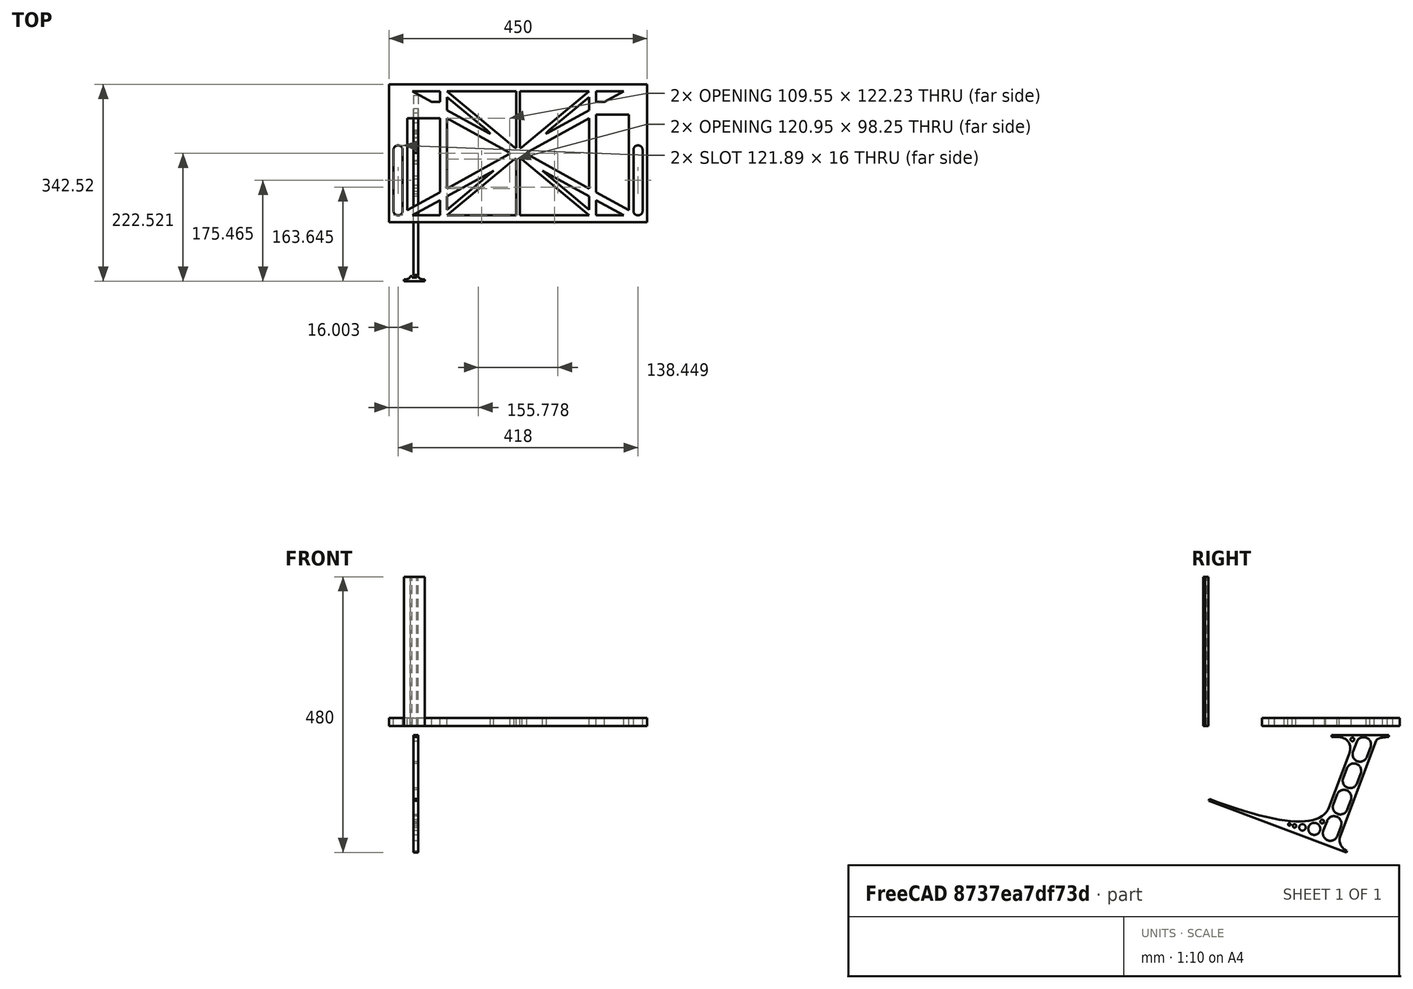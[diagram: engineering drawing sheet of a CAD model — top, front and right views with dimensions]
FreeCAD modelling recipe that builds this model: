
FCSTD DOCUMENT  (FreeCAD 0.19R0.19.2)
Label: laptopStand066
License: All rights reserved
LicenseURL: http://en.wikipedia.org/wiki/All_rights_reserved
objects: Sketcher::SketchObject×3, Part::Extrusion×3
note: 6 computed .brp shape members not serialized (recipe doc carries the construction recipe); baked Part::Feature solids carry a one-line shape summary decoded from their .brp

FEATURE [Sketcher::SketchObject] Sketch
  FullyConstrained = true
  sketch-geometry (112):
    g0: LineSegment StartX=-10.9272 StartY=-82.7794 StartZ=0 EndX=46.0728 EndY=-51.4823 EndZ=0
    g1: LineSegment StartX=366.073 StartY=-91.7794 StartZ=0 EndX=318.073 EndY=-65.424 EndZ=0
    g2: LineSegment StartX=-10.9272 StartY=77.3346 StartZ=0 EndX=-10.9272 EndY=-82.7794 EndZ=0
    g3: LineSegment StartX=375.073 StartY=-82.7794 StartZ=0 EndX=375.073 EndY=83.9235 EndZ=0
    g4: LineSegment StartX=-1.92719 StartY=-91.7794 StartZ=0 EndX=46.0728 EndY=-91.7794 EndZ=0
    g5: LineSegment StartX=318.073 StartY=124.221 StartZ=0 EndX=366.073 EndY=124.221 EndZ=0
    g6: LineSegment StartX=306.073 StartY=-81.8102 StartZ=0 EndX=224.513 EndY=-14.0532 EndZ=0
    g7: LineSegment StartX=306.073 StartY=124.221 StartZ=0 EndX=189.124 EndY=27.0628 EndZ=0
    g8: LineSegment StartX=58.0728 StartY=-91.7794 StartZ=0 EndX=175.022 EndY=5.37834 EndZ=0
    g9: LineSegment StartX=58.0728 StartY=-81.8102 StartZ=0 EndX=58.0728 EndY=-58.8351 EndZ=0
    g10: LineSegment StartX=306.073 StartY=114.251 StartZ=0 EndX=306.073 EndY=91.2763 EndZ=0
    g11: LineSegment StartX=175.022 StartY=27.0628 StartZ=0 EndX=58.0728 EndY=124.221 EndZ=0
    g12: LineSegment StartX=139.632 StartY=-14.0532 StartZ=0 EndX=58.0728 EndY=-81.8102 EndZ=0
    g13: LineSegment StartX=139.632 StartY=-14.0532 StartZ=0 EndX=58.0728 EndY=-58.8351 EndZ=0
    g14: LineSegment StartX=189.124 StartY=5.37834 StartZ=0 EndX=306.073 EndY=-91.7794 EndZ=0
    g15: LineSegment StartX=306.073 StartY=77.3346 StartZ=0 EndX=306.073 EndY=-44.8935 EndZ=0
    g16: LineSegment StartX=318.073 StartY=83.9235 StartZ=0 EndX=318.073 EndY=-51.4823 EndZ=0
    g17: LineSegment StartX=306.073 StartY=-58.8351 StartZ=0 EndX=224.513 EndY=-14.0532 EndZ=0
    g18: LineSegment StartX=306.073 StartY=-58.8351 StartZ=0 EndX=306.073 EndY=-81.8102 EndZ=0
    g19: LineSegment StartX=318.073 StartY=-51.4823 StartZ=0 EndX=375.073 EndY=-82.7794 EndZ=0
    g20: LineSegment StartX=318.073 StartY=-65.424 StartZ=0 EndX=318.073 EndY=-91.7794 EndZ=0
    g21: LineSegment StartX=318.073 StartY=-91.7794 StartZ=0 EndX=366.073 EndY=-91.7794 EndZ=0
    g22: LineSegment StartX=58.0728 StartY=-44.8935 StartZ=0 EndX=58.0728 EndY=77.3346 EndZ=0
    g23: LineSegment StartX=46.0728 StartY=-65.424 StartZ=0 EndX=-1.92719 EndY=-91.7794 EndZ=0
    g24: LineSegment StartX=46.0728 StartY=-65.424 StartZ=0 EndX=46.0728 EndY=-91.7794 EndZ=0
    g25: LineSegment StartX=58.0728 StartY=91.2763 StartZ=0 EndX=58.0728 EndY=114.251 EndZ=0
    g26: LineSegment StartX=46.0728 StartY=77.3346 StartZ=0 EndX=46.0728 EndY=-51.4823 EndZ=0
    g27: LineSegment StartX=-42.9272 StartY=136.221 StartZ=0 EndX=-42.9272 EndY=-103.779 EndZ=0
    g28: LineSegment StartX=407.073 StartY=136.221 StartZ=0 EndX=407.073 EndY=-103.779 EndZ=0
    g29: LineSegment StartX=179.022 StartY=27.0628 StartZ=0 EndX=179.022 EndY=124.221 EndZ=0
    g30: LineSegment StartX=185.124 StartY=27.0628 StartZ=0 EndX=185.124 EndY=124.221 EndZ=0
    g31: ArcOfCircle CenterX=-26.9272 CenterY=22.1087 CenterZ=0 NormalX=0 NormalY=0 NormalZ=1 AngleXU=0 Radius=8 StartAngle=1e-16 EndAngle=3.14159
    g32: ArcOfCircle CenterX=-26.9272 CenterY=-83.7794 CenterZ=0 NormalX=0 NormalY=0 NormalZ=1 AngleXU=0 Radius=8 StartAngle=3.14159 EndAngle=6.28319
    g33: LineSegment StartX=-34.9272 StartY=22.1087 StartZ=0 EndX=-34.9272 EndY=-83.7794 EndZ=0
    g34: LineSegment StartX=-18.9272 StartY=22.1087 StartZ=0 EndX=-18.9272 EndY=-83.7794 EndZ=0
    g35: LineSegment StartX=185.124 StartY=-91.7794 StartZ=0 EndX=306.073 EndY=-91.7794 EndZ=0
    g36: LineSegment StartX=179.022 StartY=-91.7794 StartZ=0 EndX=58.0728 EndY=-91.7794 EndZ=0
    g37: LineSegment StartX=306.073 StartY=124.221 StartZ=0 EndX=185.124 EndY=124.221 EndZ=0
    g38: LineSegment StartX=179.022 StartY=124.221 StartZ=0 EndX=58.0728 EndY=124.221 EndZ=0
    g39: ArcOfCircle CenterX=391.073 CenterY=22.1087 CenterZ=0 NormalX=0 NormalY=0 NormalZ=1 AngleXU=0 Radius=8 StartAngle=-4.4e-15 EndAngle=3.14159
    g40: LineSegment StartX=399.073 StartY=22.1087 StartZ=0 EndX=399.073 EndY=-83.7794 EndZ=0
    g41: LineSegment StartX=383.073 StartY=22.1087 StartZ=0 EndX=383.073 EndY=-83.7794 EndZ=0
    g42: ArcOfCircle CenterX=391.073 CenterY=-83.7794 CenterZ=0 NormalX=0 NormalY=0 NormalZ=1 AngleXU=0 Radius=8 StartAngle=3.14159 EndAngle=6.28319
    g43: Circle CenterX=175.022 CenterY=27.0628 CenterZ=0 NormalX=0 NormalY=0 NormalZ=1 AngleXU=0 Radius=1
    g44: Circle CenterX=179.022 CenterY=24.8665 CenterZ=0 NormalX=0 NormalY=0 NormalZ=1 AngleXU=0 Radius=1
    g45: Circle CenterX=179.022 CenterY=27.0628 CenterZ=0 NormalX=0 NormalY=0 NormalZ=1 AngleXU=0 Radius=1
    g46: BSplineCurve PolesCount=3 KnotsCount=2 Degree=2 IsPeriodic=0
    g47: GeomPoint X=175.022 Y=27.0628 Z=0
    g48: GeomPoint X=179.022 Y=27.0628 Z=0
    g49: Circle CenterX=189.124 CenterY=27.0628 CenterZ=0 NormalX=0 NormalY=0 NormalZ=1 AngleXU=0 Radius=1
    g50: Circle CenterX=185.124 CenterY=24.8665 CenterZ=0 NormalX=0 NormalY=0 NormalZ=1 AngleXU=0 Radius=1
    g51: Circle CenterX=185.124 CenterY=27.0628 CenterZ=0 NormalX=0 NormalY=0 NormalZ=1 AngleXU=0 Radius=1
    g52: BSplineCurve PolesCount=3 KnotsCount=2 Degree=2 IsPeriodic=0
    g53: GeomPoint X=189.124 Y=27.0628 Z=0
    g54: GeomPoint X=185.124 Y=27.0628 Z=0
    g55: Circle CenterX=175.022 CenterY=5.37834 CenterZ=0 NormalX=0 NormalY=0 NormalZ=1 AngleXU=0 Radius=1
    g56: Circle CenterX=179.022 CenterY=7.57463 CenterZ=0 NormalX=0 NormalY=0 NormalZ=1 AngleXU=0 Radius=1
    g57: Circle CenterX=179.022 CenterY=5.34704 CenterZ=0 NormalX=0 NormalY=0 NormalZ=1 AngleXU=0 Radius=1
    g58: BSplineCurve PolesCount=3 KnotsCount=2 Degree=2 IsPeriodic=0
    g59: GeomPoint X=175.022 Y=5.37834 Z=0
    g60: GeomPoint X=179.022 Y=5.34704 Z=0
    g61: Circle CenterX=189.124 CenterY=5.37834 CenterZ=0 NormalX=0 NormalY=0 NormalZ=1 AngleXU=0 Radius=1
    g62: Circle CenterX=185.124 CenterY=7.57463 CenterZ=0 NormalX=0 NormalY=0 NormalZ=1 AngleXU=0 Radius=1
    g63: Circle CenterX=185.124 CenterY=5.34704 CenterZ=0 NormalX=0 NormalY=0 NormalZ=1 AngleXU=0 Radius=1
    g64: BSplineCurve PolesCount=3 KnotsCount=2 Degree=2 IsPeriodic=0
    g65: GeomPoint X=189.124 Y=5.37834 Z=0
    g66: GeomPoint X=185.124 Y=5.34704 Z=0
    g67: LineSegment StartX=179.022 StartY=5.34704 StartZ=0 EndX=179.022 EndY=-91.7794 EndZ=0
    g68: LineSegment StartX=185.124 StartY=-91.7794 StartZ=0 EndX=185.124 EndY=5.34704 EndZ=0
    g69: Circle CenterX=165.871 CenterY=18.1458 CenterZ=0 NormalX=0 NormalY=0 NormalZ=1 AngleXU=0 Radius=1
    g70: Circle CenterX=169.377 CenterY=16.2206 CenterZ=0 NormalX=0 NormalY=0 NormalZ=1 AngleXU=0 Radius=1
    g71: Circle CenterX=165.871 CenterY=14.2954 CenterZ=0 NormalX=0 NormalY=0 NormalZ=1 AngleXU=0 Radius=1
    g72: BSplineCurve PolesCount=3 KnotsCount=2 Degree=2 IsPeriodic=0
    g73: GeomPoint X=165.871 Y=18.1458 Z=0
    g74: GeomPoint X=165.871 Y=14.2954 Z=0
    g75: Circle CenterX=198.275 CenterY=18.1458 CenterZ=0 NormalX=0 NormalY=0 NormalZ=1 AngleXU=0 Radius=1
    g76: Circle CenterX=194.768 CenterY=16.2206 CenterZ=0 NormalX=0 NormalY=0 NormalZ=1 AngleXU=0 Radius=1
    g77: Circle CenterX=198.275 CenterY=14.2954 CenterZ=0 NormalX=0 NormalY=0 NormalZ=1 AngleXU=0 Radius=1
    g78: BSplineCurve PolesCount=3 KnotsCount=2 Degree=2 IsPeriodic=0
    g79: GeomPoint X=198.275 Y=18.1458 Z=0
    g80: GeomPoint X=198.275 Y=14.2954 Z=0
    g81: LineSegment StartX=165.871 StartY=18.1458 StartZ=0 EndX=58.0728 EndY=77.3346 EndZ=0
    g82: LineSegment StartX=58.0728 StartY=-44.8935 StartZ=0 EndX=165.871 EndY=14.2954 EndZ=0
    g83: LineSegment StartX=198.275 StartY=18.1458 StartZ=0 EndX=306.073 EndY=77.3346 EndZ=0
    g84: LineSegment StartX=198.275 StartY=14.2954 StartZ=0 EndX=306.073 EndY=-44.8935 EndZ=0
    g85: LineSegment StartX=407.073 StartY=-103.779 StartZ=0 EndX=-42.9272 EndY=-103.779 EndZ=0
    g86: LineSegment StartX=407.073 StartY=136.221 StartZ=0 EndX=-42.9272 EndY=136.221 EndZ=0
    g87: LineSegment StartX=46.0728 StartY=77.3346 StartZ=0 EndX=-10.9272 EndY=77.3346 EndZ=0
    g88: LineSegment StartX=46.0728 StartY=105.865 StartZ=0 EndX=31.5028 EndY=105.865 EndZ=0
    g89: LineSegment StartX=46.0728 StartY=124.221 StartZ=0 EndX=46.0728 EndY=105.865 EndZ=0
    g90: LineSegment StartX=-1.92719 StartY=124.221 StartZ=0 EndX=31.5028 EndY=105.865 EndZ=0
    g91: LineSegment StartX=46.0728 StartY=124.221 StartZ=0 EndX=-1.92719 EndY=124.221 EndZ=0
    g92: LineSegment StartX=318.073 StartY=83.9235 StartZ=0 EndX=375.073 EndY=83.9235 EndZ=0
    g93: LineSegment StartX=318.073 StartY=105.865 StartZ=0 EndX=332.643 EndY=105.865 EndZ=0
    g94: LineSegment StartX=332.643 StartY=105.865 StartZ=0 EndX=366.073 EndY=124.221 EndZ=0
    g95: LineSegment StartX=318.073 StartY=124.221 StartZ=0 EndX=318.073 EndY=105.865 EndZ=0
    g96: Circle CenterX=125.607 CenterY=54.1951 CenterZ=0 NormalX=0 NormalY=0 NormalZ=1 AngleXU=0 Radius=1
    g97: Circle CenterX=139.632 CenterY=46.4944 CenterZ=0 NormalX=0 NormalY=0 NormalZ=1 AngleXU=0 Radius=1
    g98: Circle CenterX=127.325 CenterY=56.7187 CenterZ=0 NormalX=0 NormalY=0 NormalZ=1 AngleXU=0 Radius=1
    g99: BSplineCurve PolesCount=3 KnotsCount=2 Degree=2 IsPeriodic=0
    g100: GeomPoint X=125.607 Y=54.1951 Z=0
    g101: GeomPoint X=127.325 Y=56.7187 Z=0
    g102: LineSegment StartX=127.325 StartY=56.7187 StartZ=0 EndX=58.0728 EndY=114.251 EndZ=0
    g103: LineSegment StartX=58.0728 StartY=91.2763 StartZ=0 EndX=125.607 EndY=54.1951 EndZ=0
    g104: Circle CenterX=236.821 CenterY=56.7187 CenterZ=0 NormalX=0 NormalY=0 NormalZ=1 AngleXU=0 Radius=1
    g105: Circle CenterX=224.513 CenterY=46.4944 CenterZ=0 NormalX=0 NormalY=0 NormalZ=1 AngleXU=0 Radius=1
    g106: Circle CenterX=238.538 CenterY=54.1951 CenterZ=0 NormalX=0 NormalY=0 NormalZ=1 AngleXU=0 Radius=1
    g107: BSplineCurve PolesCount=3 KnotsCount=2 Degree=2 IsPeriodic=0
    g108: GeomPoint X=236.821 Y=56.7187 Z=0
    g109: GeomPoint X=238.538 Y=54.1951 Z=0
    g110: LineSegment StartX=236.821 StartY=56.7187 StartZ=0 EndX=306.073 EndY=114.251 EndZ=0
    g111: LineSegment StartX=238.538 StartY=54.1951 StartZ=0 EndX=306.073 EndY=91.2763 EndZ=0
  constraints (207):
    c: Horizontal(g4)
    c: Horizontal(g5)
    c: Coincident(g13,g12)
    c: Coincident(g17,g6)
    c: Tangent(g10,g15)
    c: Coincident(g18,g6)
    c: Tangent(g1,g17)
    c: Tangent(g15,g18)
    c: Coincident(g16,g19)
    c: Coincident(g20,g1)
    c: Tangent(g16,g20)
    c: Coincident(g12,g9)
    c: Tangent(g9,g22)
    c: Coincident(g13,g9)
    c: Tangent(g13,g23)
    c: Coincident(g24,g23)
    c: Coincident(g0,g26)
    c: Tangent(g22,g25)
    c: Block(g11)
    c: Block(g7)
    c: Block(g19)
    c: Block(g3)
    c: Block(g17)
    c: Block(g18)
    c: Block(g1)
    c: Block(g20)
    c: Block(g14)
    c: Block(g8)
    c: Block(g13)
    c: Block(g12)
    c: Block(g24)
    c: Block(g23)
    c: Block(g0)
    c: Block(g2)
    c: Block(g25)
    c: Block(g15)
    c: Block(g5)
    c: Block(g21)
    c: Block(g4)
    c: Vertical(g27)
    c: Vertical(g28)
    c: Block(g28)
    c: Block(g27)
    c: Vertical(g29)
    c: Vertical(g30)
    c: Block(g29)
    c: Block(g30)
    c: Tangent(g31,g34) = 1.5708
    c: Tangent(g31,g33) = -1.5708
    c: Tangent(g33,g32) = -1.5708
    c: Tangent(g34,g32) = 1.5708
    c: Vertical(g33)
    c: Equal(g31,g32)
    c: Block(g34)
    c: Block(g33)
    c: Coincident(g35,g14)
    c: Horizontal(g35)
    c: Coincident(g36,g8)
    c: Horizontal(g36)
    c: Coincident(g37,g7)
    c: Coincident(g37,g30)
    c: Horizontal(g37)
    c: Coincident(g38,g29)
    c: Coincident(g38,g11)
    c: Horizontal(g38)
    c: Tangent(g39,g40) = 1.5708
    c: Tangent(g40,g42) = 1.5708
    c: Equal(g39,g42)
    c: Coincident(g41,g39)
    c: Coincident(g41,g42)
    c: Block(g40)
    c: Block(g41)
    c: Coincident(g46,g11)
    c: Weight(g43) = 1
    c: Equal(g43,g44)
    c: Equal(g43,g45)
    c: Coincident(g46,g29)
    c: InternalAlignment(g43,g46)
    c: InternalAlignment(g44,g46)
    c: InternalAlignment(g45,g46)
    c: InternalAlignment(g47,g46)
    c: InternalAlignment(g48,g46)
    c: Coincident(g52,g7)
    c: Weight(g49) = 1
    c: Equal(g49,g50)
    c: Equal(g49,g51)
    c: Coincident(g52,g30)
    c: InternalAlignment(g49,g52)
    c: InternalAlignment(g50,g52)
    c: InternalAlignment(g51,g52)
    c: InternalAlignment(g53,g52)
    c: InternalAlignment(g54,g52)
    c: Block(g52)
    c: Block(g46)
    c: Coincident(g58,g8)
    c: Weight(g55) = 1
    c: Equal(g55,g56)
    c: Equal(g55,g57)
    c: InternalAlignment(g55,g58)
    c: InternalAlignment(g56,g58)
    c: InternalAlignment(g57,g58)
    c: InternalAlignment(g59,g58)
    c: InternalAlignment(g60,g58)
    c: Weight(g61) = 1
    c: Equal(g61,g62)
    c: Equal(g61,g63)
    c: InternalAlignment(g61,g64)
    c: InternalAlignment(g62,g64)
    c: InternalAlignment(g63,g64)
    c: InternalAlignment(g65,g64)
    c: InternalAlignment(g66,g64)
    c: Block(g64)
    c: Block(g58)
    c: Coincident(g67,g58)
    c: Coincident(g67,g36)
    c: Vertical(g67)
    c: Coincident(g68,g35)
    c: Coincident(g68,g64)
    c: Vertical(g68)
    c: Weight(g69) = 1
    c: Equal(g69,g70)
    c: Equal(g69,g71)
    c: InternalAlignment(g69,g72)
    c: InternalAlignment(g70,g72)
    c: InternalAlignment(g71,g72)
    c: InternalAlignment(g73,g72)
    c: InternalAlignment(g74,g72)
    c: Weight(g75) = 1
    c: Equal(g75,g76)
    c: Equal(g75,g77)
    c: InternalAlignment(g75,g78)
    c: InternalAlignment(g76,g78)
    c: InternalAlignment(g77,g78)
    c: InternalAlignment(g79,g78)
    c: InternalAlignment(g80,g78)
    c: Block(g72)
    c: Block(g78)
    c: Coincident(g81,g72)
    c: Coincident(g81,g22)
    c: Coincident(g82,g22)
    c: Coincident(g82,g72)
    c: Coincident(g83,g78)
    c: Coincident(g83,g15)
    c: Coincident(g84,g78)
    c: Coincident(g84,g15)
    c: Block(g22)
    c: Coincident(g85,g28)
    c: Coincident(g85,g27)
    c: Horizontal(g85)
    c: Distance(g85) = 450
    c: Coincident(g86,g28)
    c: Coincident(g86,g27)
    c: Horizontal(g86)
    c: Horizontal(g87)
    c: Coincident(g26,g87)
    c: Horizontal(g88)
    c: Vertical(g89)
    c: Block(g89)
    c: Block(g88)
    c: Block(g87)
    c: Distance(g89) = 18.3554
    c: Coincident(g91,g89)
    c: Coincident(g91,g90)
    c: Horizontal(g91)
    c: Block(g91)
    c: Block(g90)
    c: Coincident(g88,g90)
    c: Coincident(g2,g87)
    c: Coincident(g92,g16)
    c: Horizontal(g92)
    c: Horizontal(g93)
    c: Block(g92)
    c: Block(g10)
    c: Coincident(g94,g5)
    c: Coincident(g95,g5)
    c: Coincident(g95,g93)
    c: Vertical(g95)
    c: Block(g95)
    c: Coincident(g93,g94)
    c: Block(g94)
    c: Coincident(g3,g92)
    c: Weight(g96) = 1
    c: Equal(g96,g97)
    c: Equal(g96,g98)
    c: InternalAlignment(g96,g99)
    c: InternalAlignment(g97,g99)
    c: InternalAlignment(g98,g99)
    c: InternalAlignment(g100,g99)
    c: InternalAlignment(g101,g99)
    c: Block(g99)
    c: Coincident(g102,g99)
    c: Coincident(g102,g25)
    c: Coincident(g103,g25)
    c: Coincident(g103,g99)
    c: Weight(g104) = 1
    c: Equal(g104,g105)
    c: Equal(g104,g106)
    c: InternalAlignment(g104,g107)
    c: InternalAlignment(g105,g107)
    c: InternalAlignment(g106,g107)
    c: InternalAlignment(g108,g107)
    c: InternalAlignment(g109,g107)
    c: Block(g107)
    c: Coincident(g110,g107)
    c: Coincident(g110,g10)
    c: Coincident(g111,g107)
    c: Coincident(g111,g10)
FEATURE [Sketcher::SketchObject] Sketch001
  FullyConstrained = true
  MapMode = 4
  Placement = pos=(0,0,0) rot=(0.57735,0.57735,0.57735;2.0944rad)
  Support = -> [Sketch]
  sketch-geometry (46):
    g0: BSplineCurve PolesCount=3 KnotsCount=2 Degree=2 IsPeriodic=0
    g1: ArcOfCircle CenterX=73.1223 CenterY=-32.291 CenterZ=0 NormalX=0 NormalY=0 NormalZ=1 AngleXU=0 Radius=13 StartAngle=5.92268 EndAngle=9.06428
    g2: ArcOfCircle CenterX=66.7816 CenterY=-49.1439 CenterZ=0 NormalX=0 NormalY=0 NormalZ=1 AngleXU=0 Radius=13 StartAngle=2.78068 EndAngle=5.92131
    g3: ArcOfCircle CenterX=55.9263 CenterY=-78.1807 CenterZ=0 NormalX=0 NormalY=0 NormalZ=1 AngleXU=0 Radius=13 StartAngle=5.92268 EndAngle=9.06428
    g4: ArcOfCircle CenterX=49.5884 CenterY=-95.0342 CenterZ=0 NormalX=0 NormalY=0 NormalZ=1 AngleXU=0 Radius=13 StartAngle=2.78068 EndAngle=5.92131
    g5: ArcOfCircle CenterX=38.7206 CenterY=-124.067 CenterZ=0 NormalX=0 NormalY=0 NormalZ=1 AngleXU=0 Radius=13 StartAngle=5.92268 EndAngle=9.06428
    g6: ArcOfCircle CenterX=32.3875 CenterY=-140.92 CenterZ=0 NormalX=0 NormalY=0 NormalZ=1 AngleXU=0 Radius=13 StartAngle=2.78068 EndAngle=5.92131
    g7: ArcOfCircle CenterX=21.4715 CenterY=-169.934 CenterZ=0 NormalX=0 NormalY=0 NormalZ=1 AngleXU=0 Radius=13 StartAngle=5.92268 EndAngle=9.06428
    g8: ArcOfCircle CenterX=15.1336 CenterY=-186.787 CenterZ=0 NormalX=0 NormalY=0 NormalZ=1 AngleXU=0 Radius=13 StartAngle=2.78068 EndAngle=5.92131
    g9-g12: Circle x4 (B-spline internal-alignment scaffolding for g13; pole/knot coordinates omitted)
    g13: BSplineCurve PolesCount=4 KnotsCount=2 Degree=3 IsPeriodic=0
    g14: GeomPoint X=28.8094 Y=-19.0875 Z=0
    g15: GeomPoint X=47.0443 Y=-50.4712 Z=0
    g16: Circle CenterX=53.5586 CenterY=-23.2695 CenterZ=0 NormalX=0 NormalY=0 NormalZ=1 AngleXU=0 Radius=3.24518
    g17: Circle CenterX=-195.441 CenterY=-127.082 CenterZ=0 NormalX=0 NormalY=0 NormalZ=1 AngleXU=0 Radius=1
    g18: Circle CenterX=-8.24091 CenterY=-197.481 CenterZ=0 NormalX=0 NormalY=0 NormalZ=1 AngleXU=0 Radius=1
    g19: Circle CenterX=12.8789 CenterY=-141.321 CenterZ=0 NormalX=0 NormalY=0 NormalZ=1 AngleXU=0 Radius=1
    g20: BSplineCurve PolesCount=3 KnotsCount=2 Degree=2 IsPeriodic=0
    g21: GeomPoint X=-195.441 Y=-127.082 Z=0
    g22: GeomPoint X=12.8789 Y=-141.321 Z=0
    g23: Circle CenterX=-12.8016 CenterY=-179.036 CenterZ=0 NormalX=0 NormalY=0 NormalZ=1 AngleXU=0 Radius=10.5072
    g24: Circle CenterX=0.933922 CenterY=-166.43 CenterZ=0 NormalX=0 NormalY=0 NormalZ=1 AngleXU=0 Radius=3.26661
    g25: Circle CenterX=-33.5518 CenterY=-176.44 CenterZ=0 NormalX=0 NormalY=0 NormalZ=1 AngleXU=0 Radius=5.64388
    g26: Circle CenterX=-47.2366 CenterY=-173.859 CenterZ=0 NormalX=0 NormalY=0 NormalZ=1 AngleXU=0 Radius=3.01653
    g27: Circle CenterX=-56.2595 CenterY=-171.456 CenterZ=0 NormalX=0 NormalY=0 NormalZ=1 AngleXU=0 Radius=2.12826
    g28: ArcOfCircle CenterX=51.2151 CenterY=-198.473 CenterZ=0 NormalX=0 NormalY=0 NormalZ=1 AngleXU=0 Radius=20 StartAngle=2.78189 EndAngle=4.35269
    g29: LineSegment StartX=32.4951 StartY=-191.433 StartZ=0 EndX=94.6578 EndY=-26.1352 EndZ=0
    g30: LineSegment StartX=43.1192 StartY=-220.001 StartZ=0 EndX=-196.497 EndY=-129.89 EndZ=0
    g31: LineSegment StartX=43.1192 StartY=-220.001 StartZ=0 EndX=44.1752 EndY=-217.193 EndZ=0
    g32: LineSegment StartX=117.223 StartY=-19.0875 StartZ=0 EndX=117.223 EndY=-16.0875 EndZ=0
    g33: LineSegment StartX=117.223 StartY=-16.0875 StartZ=0 EndX=17.2232 EndY=-16.0875 EndZ=0
    g34: LineSegment StartX=17.2232 StartY=-16.0875 StartZ=0 EndX=17.2232 EndY=-19.0875 EndZ=0
    g35: LineSegment StartX=28.8094 StartY=-19.0875 StartZ=0 EndX=17.2232 EndY=-19.0875 EndZ=0
    g36: LineSegment StartX=47.0443 StartY=-50.4712 StartZ=0 EndX=12.8789 EndY=-141.321 EndZ=0
    g37: LineSegment StartX=-195.441 StartY=-127.082 StartZ=0 EndX=-196.497 EndY=-129.89 EndZ=0
    g38: LineSegment StartX=85.2866 StartY=-36.8766 StartZ=0 EndX=78.9396 EndY=-53.7463 EndZ=0
    g39: LineSegment StartX=60.9579 StartY=-27.7053 StartZ=0 EndX=54.6191 EndY=-44.5532 EndZ=0
    g40: LineSegment StartX=68.0907 StartY=-82.7664 StartZ=0 EndX=61.7465 EndY=-99.6365 EndZ=0
    g41: LineSegment StartX=43.7619 StartY=-73.595 StartZ=0 EndX=37.426 EndY=-90.4435 EndZ=0
    g42: LineSegment StartX=50.885 StartY=-128.652 StartZ=0 EndX=44.5456 EndY=-145.522 EndZ=0
    g43: LineSegment StartX=26.5562 StartY=-119.481 StartZ=0 EndX=20.2251 EndY=-136.329 EndZ=0
    g44: LineSegment StartX=9.3071 StartY=-165.349 StartZ=0 EndX=2.97115 EndY=-182.197 EndZ=0
    g45: LineSegment StartX=33.6358 StartY=-174.52 StartZ=0 EndX=27.2917 EndY=-191.39 EndZ=0
  constraints (71):
    c: Block(g0)
    c: Block(g1)
    c: Block(g2)
    c: Block(g4)
    c: Block(g3)
    c: Block(g6)
    c: Block(g5)
    c: Block(g8)
    c: Block(g7)
    c: Weight(g9) = 1
    c: Equal(g9,g10)
    c: Equal(g9,g11)
    c: Equal(g9,g12)
    c: InternalAlignment(g9-g12 -> g13) x4
    c: InternalAlignment(g14,g13)
    c: InternalAlignment(g15,g13)
    c: Block(g16)
    c: Weight(g17) = 1
    c: Equal(g17,g18)
    c: Equal(g17,g19)
    c: InternalAlignment(g17,g20)
    c: InternalAlignment(g18,g20)
    c: InternalAlignment(g19,g20)
    c: InternalAlignment(g21,g20)
    c: InternalAlignment(g22,g20)
    c: Block(g20)
    c: Block(g23)
    c: Block(g24)
    c: Block(g25)
    c: Block(g26)
    c: Block(g27)
    c: Block(g28)
    c: Coincident(g29,g28)
    c: Coincident(g29,g0)
    c: Block(g13)
    c: Coincident(g31,g30)
    c: Coincident(g31,g28)
    c: Block(g31)
    c: Coincident(g32,g0)
    c: Vertical(g32)
    c: Coincident(g33,g32)
    c: Horizontal(g33)
    c: Coincident(g34,g33)
    c: Vertical(g34)
    c: Block(g33)
    c: Coincident(g35,g13)
    c: Coincident(g35,g34)
    c: Horizontal(g35)
    c: Coincident(g36,g13)
    c: Coincident(g36,g20)
    c: Coincident(g37,g20)
    c: Coincident(g37,g30)
    c: Block(g30)
    c: Coincident(g38,g1)
    c: Coincident(g38,g2)
    c: Coincident(g39,g1)
    c: Coincident(g39,g2)
    c: Coincident(g40,g3)
    c: Coincident(g40,g4)
    c: Coincident(g41,g3)
    c: Coincident(g41,g4)
    c: Coincident(g42,g5)
    c: Coincident(g42,g6)
    c: Coincident(g43,g5)
    c: Coincident(g43,g6)
    c: Coincident(g44,g7)
    c: Coincident(g44,g8)
    c: Coincident(g45,g7)
    c: Coincident(g45,g8)
    c: Distance(g30) = 256
    c: Distance(g33) = 100
FEATURE [Part::Extrusion] Extrude002
  Base = -> Sketch001
  Dir = (1,0,0)
  DirMode = 2
  FaceMakerClass = Part::FaceMakerBullseye
  LengthFwd = 8
  LengthRev = 0
  Solid = true
  Symmetric = false
FEATURE [Sketcher::SketchObject] Sketch002
  FullyConstrained = true
  sketch-geometry (20):
    g0: LineSegment StartX=-2.77179 StartY=-200.304 StartZ=0 EndX=5.22821 EndY=-200.304 EndZ=0
    g1: LineSegment StartX=5.22821 StartY=-200.304 StartZ=0 EndX=5.22821 EndY=-197.304 EndZ=0
    g2: LineSegment StartX=-2.77179 StartY=-200.304 StartZ=0 EndX=-2.77179 EndY=-197.304 EndZ=0
    g3: LineSegment StartX=5.22821 StartY=-197.304 StartZ=0 EndX=8.22821 EndY=-197.304 EndZ=0
    g4: LineSegment StartX=-2.77179 StartY=-197.304 StartZ=0 EndX=-5.77179 EndY=-197.304 EndZ=0
    g5: LineSegment StartX=19.2282 StartY=-203.304 StartZ=0 EndX=19.2282 EndY=-206.304 EndZ=0
    g6: LineSegment StartX=-16.7718 StartY=-203.304 StartZ=0 EndX=-16.7718 EndY=-206.304 EndZ=0
    g7: LineSegment StartX=-16.7718 StartY=-206.304 StartZ=0 EndX=19.2282 EndY=-206.304 EndZ=0
    g8: Circle CenterX=-16.7718 CenterY=-203.304 CenterZ=0 NormalX=0 NormalY=0 NormalZ=1 AngleXU=0 Radius=1
    g9: Circle CenterX=-5.77179 CenterY=-203.304 CenterZ=0 NormalX=0 NormalY=0 NormalZ=1 AngleXU=0 Radius=1
    g10: Circle CenterX=-5.77179 CenterY=-197.304 CenterZ=0 NormalX=0 NormalY=0 NormalZ=1 AngleXU=0 Radius=1
    g11: BSplineCurve PolesCount=3 KnotsCount=2 Degree=2 IsPeriodic=0
    g12: GeomPoint X=-16.7718 Y=-203.304 Z=0
    g13: GeomPoint X=-5.77179 Y=-197.304 Z=0
    g14: Circle CenterX=19.2282 CenterY=-203.304 CenterZ=0 NormalX=0 NormalY=0 NormalZ=1 AngleXU=0 Radius=1
    g15: Circle CenterX=8.22821 CenterY=-203.304 CenterZ=0 NormalX=0 NormalY=0 NormalZ=1 AngleXU=0 Radius=1
    g16: Circle CenterX=8.22821 CenterY=-197.304 CenterZ=0 NormalX=0 NormalY=0 NormalZ=1 AngleXU=0 Radius=1
    g17: BSplineCurve PolesCount=3 KnotsCount=2 Degree=2 IsPeriodic=0
    g18: GeomPoint X=19.2282 Y=-203.304 Z=0
    g19: GeomPoint X=8.22821 Y=-197.304 Z=0
  constraints (41):
    c: Horizontal(g0)
    c: Distance(g0) = 8
    c: Coincident(g1,g0)
    c: Vertical(g1)
    c: Distance(g1) = 3
    c: Coincident(g2,g0)
    c: Vertical(g2)
    c: Distance(g2) = 3
    c: Coincident(g3,g1)
    c: Horizontal(g3)
    c: Distance(g3) = 3
    c: Coincident(g4,g2)
    c: Horizontal(g4)
    c: Distance(g4) = 3
    c: Vertical(g5)
    c: Vertical(g6)
    c: Coincident(g7,g6)
    c: Coincident(g7,g5)
    c: Weight(g8) = 1
    c: Equal(g8,g9)
    c: Equal(g8,g10)
    c: Coincident(g11,g4)
    c: InternalAlignment(g8,g11)
    c: InternalAlignment(g9,g11)
    c: InternalAlignment(g10,g11)
    c: InternalAlignment(g12,g11)
    c: InternalAlignment(g13,g11)
    c: Coincident(g17,g5)
    c: Weight(g14) = 1
    c: Equal(g14,g15)
    c: Equal(g14,g16)
    c: Coincident(g17,g3)
    c: InternalAlignment(g14,g17)
    c: InternalAlignment(g15,g17)
    c: InternalAlignment(g16,g17)
    c: InternalAlignment(g18,g17)
    c: InternalAlignment(g19,g17)
    c: Block(g7)
    c: Block(g17)
    c: Block(g11)
    c: Block(g6)
FEATURE [Part::Extrusion] Extrude003
  Base = -> Sketch002
  Dir = (0,0,1)
  DirMode = 2
  FaceMakerClass = Part::FaceMakerBullseye
  LengthFwd = 260
  LengthRev = 0
  Solid = true
  Symmetric = false
FEATURE [Part::Extrusion] Extrude
  Base = -> Sketch
  Dir = (0,0,1)
  DirMode = 2
  FaceMakerClass = Part::FaceMakerBullseye
  LengthFwd = 14
  LengthRev = 0
  Solid = true
  Symmetric = false
